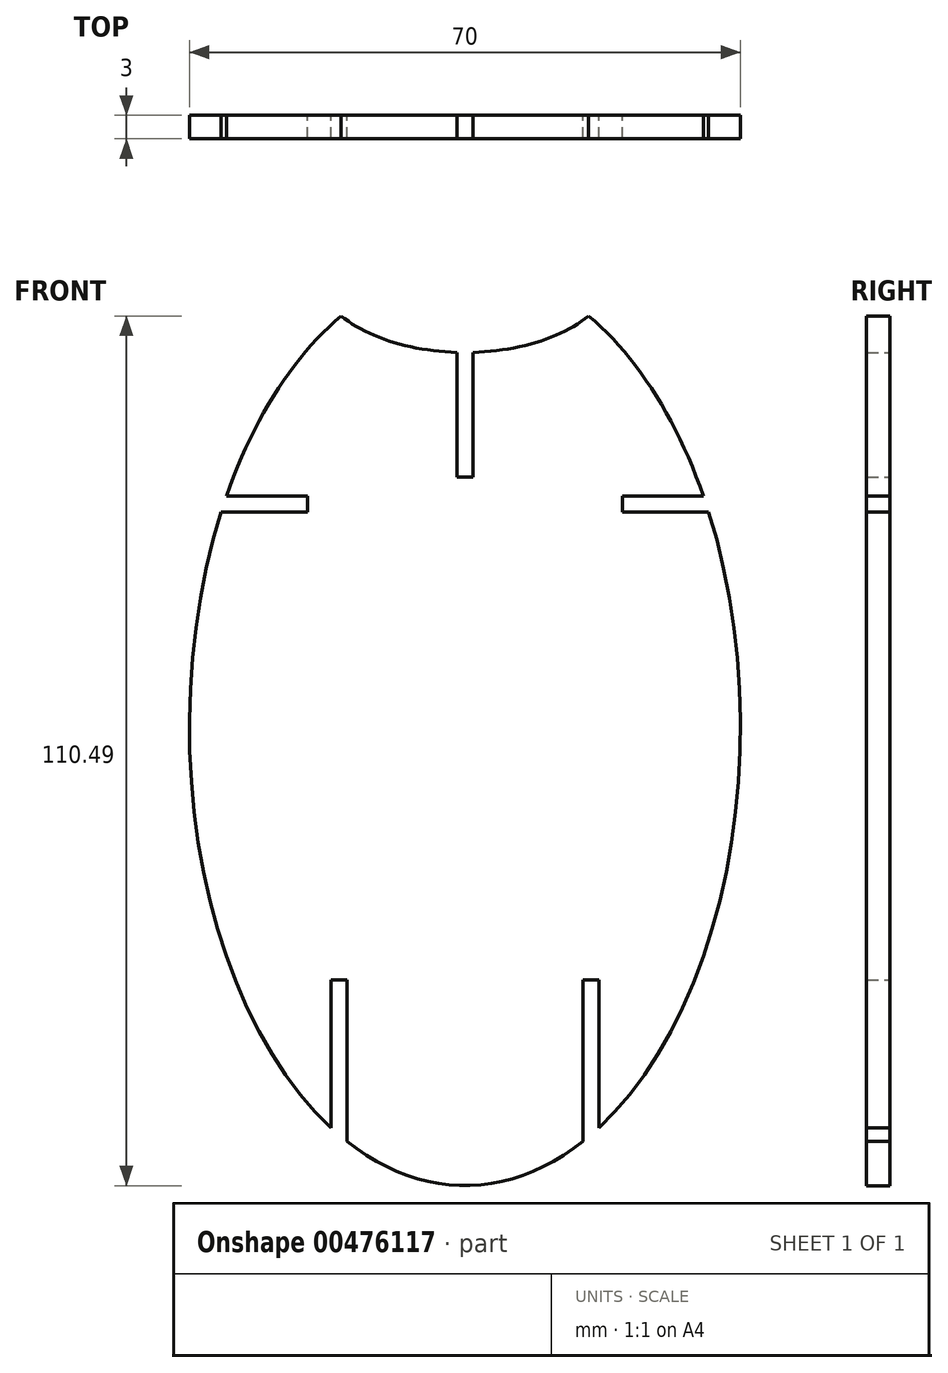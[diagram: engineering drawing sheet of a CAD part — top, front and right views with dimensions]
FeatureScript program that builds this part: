
annotation { "Feature Type Name" : "Feature", "Feature Type Description" : "" }
export const myFeature = defineFeature(function(context is Context, id is Id, definition is map)
    precondition{}
    {
        {
            var Q0;
            Q0=qCreatedBy(makeId("Front.planeOp"),FACE);
            var sketch = newSketch(context, id + "F0", { "sketchPlane" : qUnion([Q0])});
            skEllipse(sketch, "E0", {"center": v(0, 0) * mm, "majorRadius": 58.35 * mm, "minorRadius": 35 * mm, "majorAxis": v(0, -1)});
            skSolve(sketch);
        }
        {
            var Q0;
            Q0 = qSketchRegion(id + "F0", true);
            extrude(context, id + "F1", {"entities" : qUnion([Q0]), "depth" : 3 * mm});
        }
        {
            var Q0;
            Q0=qCreatedBy(makeId("Front.planeOp"),FACE);
            var sketch = newSketch(context, id + "F2", { "sketchPlane" : qUnion([Q0])});
            skLineSegment(sketch, "E1.bottom", {"start": v(-49.47, 29.24) * mm, "end": v(-20, 29.24) * mm});
            skLineSegment(sketch, "E1.top", {"start": v(-49.47, 27.24) * mm, "end": v(-20, 27.24) * mm});
            skLineSegment(sketch, "E1.left", {"start": v(-49.47, 29.24) * mm, "end": v(-49.47, 27.24) * mm});
            skLineSegment(sketch, "E1.right", {"start": v(-20, 29.24) * mm, "end": v(-20, 27.24) * mm});
            skLineSegment(sketch, "E2.MirrorCS", {"start": v(49.47, 29.24) * mm, "end": v(20, 29.24) * mm});
            skLineSegment(sketch, "E3.MirrorCS", {"start": v(49.47, 27.24) * mm, "end": v(20, 27.24) * mm});
            skLineSegment(sketch, "E4.MirrorCS", {"start": v(20, 29.24) * mm, "end": v(20, 27.24) * mm});
            skLineSegment(sketch, "E5.MirrorCS", {"start": v(49.47, 29.24) * mm, "end": v(49.47, 27.24) * mm});
            skSolve(sketch);
        }
        {
            var Q0;
            Q0 = qSketchRegion(id + "F2", true);
            extrude(context, id + "F3", {"entities" : qUnion([Q0]), "operationType" : NewBodyOperationType.REMOVE, "depth" : 25 * mm});
        }
        {
            var Q0;
            Q0=qCreatedBy(makeId("Front.planeOp"),FACE);
            var sketch = newSketch(context, id + "F4", { "sketchPlane" : qUnion([Q0])});
            skLineSegment(sketch, "E6.bottom", {"start": v(-17, -32.19) * mm, "end": v(-15, -32.19) * mm});
            skLineSegment(sketch, "E6.left", {"start": v(-17, -32.19) * mm, "end": v(-17, -51.2) * mm});
            skLineSegment(sketch, "E6.right", {"start": v(-15, -32.19) * mm, "end": v(-15, -53.12) * mm});
            skLineSegment(sketch, "E7.MirrorCS", {"start": v(17, -32.19) * mm, "end": v(17, -51.2) * mm});
            skLineSegment(sketch, "E8.MirrorCS", {"start": v(15, -32.19) * mm, "end": v(15, -53.12) * mm});
            skLineSegment(sketch, "E9.MirrorCS", {"start": v(17, -32.19) * mm, "end": v(15, -32.19) * mm});
            skLineSegment(sketch, "E10", {"start": v(-17, -51.2) * mm, "end": v(-17, -64.54) * mm});
            skLineSegment(sketch, "E11", {"start": v(-15, -53.12) * mm, "end": v(-15, -64.63) * mm});
            skLineSegment(sketch, "E12", {"start": v(15, -53.12) * mm, "end": v(15, -64.63) * mm});
            skLineSegment(sketch, "E13", {"start": v(17, -51.2) * mm, "end": v(17, -64.63) * mm});
            skLineSegment(sketch, "E14", {"start": v(-17, -64.54) * mm, "end": v(-15, -64.63) * mm});
            skLineSegment(sketch, "E15", {"start": v(15, -64.63) * mm, "end": v(17, -64.63) * mm});
            skSolve(sketch);
        }
        {
            var Q0;
            Q0 = qSketchRegion(id + "F4", true);
            extrude(context, id + "F5", {"entities" : qUnion([Q0]), "operationType" : NewBodyOperationType.REMOVE, "depth" : 10 * mm});
        }
        {
            var Q0;
            Q0=qCreatedBy(makeId("Front.planeOp"),FACE);
            var sketch = newSketch(context, id + "F6", { "sketchPlane" : qUnion([Q0])});
            skEllipse(sketch, "E16", {"center": v(0, 58.2) * mm, "majorRadius": 19.07 * mm, "minorRadius": 10.7 * mm, "majorAxis": v(1, 0)});
            skSolve(sketch);
        }
        {
            var Q0;
            Q0 = qSketchRegion(id + "F6", true);
            extrude(context, id + "F7", {"entities" : qUnion([Q0]), "operationType" : NewBodyOperationType.REMOVE, "depth" : 25 * mm});
        }
        {
            var Q0;
            Q0=qCreatedBy(makeId("Front.planeOp"),FACE);
            var sketch = newSketch(context, id + "F8", { "sketchPlane" : qUnion([Q0])});
            skLineSegment(sketch, "E17.bottom", {"start": v(-1, 56.7) * mm, "end": v(0, 56.7) * mm});
            skLineSegment(sketch, "E17.top", {"start": v(-1, 31.7) * mm, "end": v(0, 31.7) * mm});
            skLineSegment(sketch, "E17.left", {"start": v(-1, 56.7) * mm, "end": v(-1, 31.7) * mm});
            skLineSegment(sketch, "E17.right", {"start": v(0, 56.7) * mm, "end": v(0, 31.7) * mm});
            skLineSegment(sketch, "E18.MirrorCS", {"start": v(1, 31.7) * mm, "end": v(0, 31.7) * mm});
            skLineSegment(sketch, "E19.MirrorCS", {"start": v(1, 56.7) * mm, "end": v(1, 31.7) * mm});
            skLineSegment(sketch, "E20.MirrorCS", {"start": v(1, 56.7) * mm, "end": v(0, 56.7) * mm});
            skSolve(sketch);
        }
        {
            var Q0;
            Q0 = qSketchRegion(id + "F8", true);
            extrude(context, id + "F9", {"entities" : qUnion([Q0]), "operationType" : NewBodyOperationType.REMOVE, "depth" : 25 * mm});
        }
    });
